# Revit family: Rohrschelle Trabant Inox, M 8-M10, Gummi, V4A
name_source: partatom
category: HLS-Bauteile
revit_build: Autodesk Revit 2017 (Build: 20190507_1515(x64)
units: mm (PartAtom-declared; Revit-internal decimal feet)

## family parameters
Arbeitsebenenbasiert = Ja
Beim Laden mit Abzugskörper schneiden = Nein
Bemaßung runder Anschluss = Durchmesser verwenden
Gemeinsam genutzt = Ja
Immer vertikal = Nein
Raumberechnungspunkt = Nein
Teiletyp = Normal

## types (11) — shared parameters
Anschluss = M8/M10
Bauart = zweiteilig
Baustoffklasse = B2
DS = 5 mm  [stored 0.0164042 ft]
DVS = 5 mm  [stored 0.0164042 ft]
Dämmstärke = 5 mm  [stored 0.0164042 ft]
Fabrikat = MEFA
Farbe Schalldämmeinlage = schwarz
Firma = MEFA Befestigungs- und Montagesysteme GmbH
H1 = 2 mm  [stored 0.00656168 ft]
HGA = 17 mm
Material = Edelstahl
Material Schalldämmeinlage = TPE
Mengeneinheit = St
Schalldämmeinlage = Gummi
Verschluss = Rastverschluss
Verschluss-Schraube = M6
Vorgabe-Ansicht = 1219 mm
max. Temperaturbeständigkeit = 100 °C
max. zul. Last horizontal = 0.00 kN
max. zul. Last vertikal = 0.00 kN
zero-valued in all types: Nennweite DN Rohr, Rohraußendurchmesser

## per-type parameters (varying)
- Trabant Inox, M8/M10, Ø 12- 15, Gummi, V4A: A=23 mm  [stored 0.0754593 ft]; AB=3 mm  [stored 0.00984252 ft]; Achsabstand=42 mm; Anschlußhöhe=22 mm; Artikelnummer=051003015; B=59 mm; Breite Material=20 mm; D=15 mm  [stored 0.0492126 ft]; D0=24 mm  [stored 0.0787402 ft]; DF1=17 mm; DF2=16 mm  [stored 0.0524934 ft]; Dmax=15 mm  [stored 0.0492126 ft]; Dmin=12 mm  [stored 0.0393701 ft]; EAN=4250928453839; Gewicht=0.05 kg; Gewicht pro Bauteil=0.05 kg; H=43 mm  [stored 0.141076 ft]; H2=4 mm  [stored 0.0131234 ft]; Kurztext1=Rohrschelle Trabant Inox 20x1,0; Kurztext2=12 - 15 mm M8/M10 TPE; MB=20 mm  [stored 0.0656168 ft]; MD=1 mm  [stored 0.00328084 ft]; Materialmaße=20x1,0 mm; R=12 mm  [stored 0.0393701 ft]; RM=15 mm  [stored 0.0492126 ft]; S=42 mm  [stored 0.137795 ft]; Stärke Material=1 mm  [stored 0.00328084 ft]; max. Rohraußendurchmesser=15 mm  [stored 0.0492126 ft]; min. Rohraußendurchmesser=12 mm  [stored 0.0393701 ft]; vpe=100 St
- Trabant Inox, M8/M10, Ø 16- 20, Gummi, V4A: A=23 mm  [stored 0.0754593 ft]; AB=4 mm  [stored 0.0131234 ft]; Achsabstand=46,5 mm; Anschlußhöhe=22 mm; Artikelnummer=051003020; B=64 mm; Breite Material=20 mm; D=20 mm  [stored 0.0656168 ft]; D0=29 mm  [stored 0.0951444 ft]; DF1=17 mm; DF2=16 mm  [stored 0.0524934 ft]; Dmax=20 mm  [stored 0.0656168 ft]; Dmin=16 mm  [stored 0.0524934 ft]; EAN=4250928453846; Gewicht=0.05 kg; Gewicht pro Bauteil=0.05 kg; H=48 mm  [stored 0.15748 ft]; H2=5 mm  [stored 0.0164042 ft]; Kurztext1=Rohrschelle Trabant Inox 20x1,0; Kurztext2=16 - 20 mm M8/M10 TPE; MB=20 mm  [stored 0.0656168 ft]; MD=1 mm  [stored 0.00328084 ft]; Materialmaße=20x1,0 mm; R=15 mm  [stored 0.0492126 ft]; RM=18 mm  [stored 0.0590551 ft]; Rohraußendurchmesser Zoll=3/8 Zoll; S=47 mm  [stored 0.154199 ft]; Stärke Material=1 mm  [stored 0.00328084 ft]; max. Rohraußendurchmesser=20 mm  [stored 0.0656168 ft]; min. Rohraußendurchmesser=16 mm  [stored 0.0524934 ft]; vpe=100 St
- Trabant Inox, M8/M10, Ø 21- 25, Gummi, V4A: A=23 mm  [stored 0.0754593 ft]; AB=4 mm  [stored 0.0131234 ft]; Achsabstand=51,5 mm; Anschlußhöhe=22 mm; Artikelnummer=051003025; B=69 mm; Breite Material=20 mm; D=25 mm  [stored 0.082021 ft]; D0=34 mm; DF1=17 mm; DF2=16 mm  [stored 0.0524934 ft]; Dmax=25 mm  [stored 0.082021 ft]; Dmin=21 mm  [stored 0.0688976 ft]; EAN=4250928453853; Gewicht=0.06 kg; Gewicht pro Bauteil=0.06 kg; H=53 mm  [stored 0.173885 ft]; H2=5 mm  [stored 0.0164042 ft]; Kurztext1=Rohrschelle Trabant Inox 20x1,0; Kurztext2=21 - 25 mm M8/M10 TPE; MB=20 mm  [stored 0.0656168 ft]; MD=1 mm  [stored 0.00328084 ft]; Materialmaße=20x1,0 mm; R=17 mm; RM=20 mm  [stored 0.0656168 ft]; Rohraußendurchmesser Zoll=1/2 Zoll; S=52 mm; Stärke Material=1 mm  [stored 0.00328084 ft]; max. Rohraußendurchmesser=25 mm  [stored 0.082021 ft]; min. Rohraußendurchmesser=21 mm  [stored 0.0688976 ft]; vpe=100 St
- Trabant Inox, M8/M10, Ø 26- 30, Gummi, V4A: A=23 mm  [stored 0.0754593 ft]; AB=4 mm  [stored 0.0131234 ft]; Achsabstand=57,0 mm; Anschlußhöhe=22 mm; Artikelnummer=051003030; B=74 mm; Breite Material=20 mm; D=30 mm  [stored 0.0984252 ft]; D0=39 mm  [stored 0.127953 ft]; DF1=17 mm; DF2=16 mm  [stored 0.0524934 ft]; Dmax=30 mm  [stored 0.0984252 ft]; Dmin=26 mm; EAN=4250928453860; Gewicht=0.06 kg; Gewicht pro Bauteil=0.06 kg; H=58 mm; H2=5 mm  [stored 0.0164042 ft]; Kurztext1=Rohrschelle Trabant Inox 20x1,0; Kurztext2=26 - 30 mm M8/M10 TPE; MB=20 mm  [stored 0.0656168 ft]; MD=1 mm  [stored 0.00328084 ft]; Materialmaße=20x1,0 mm; R=20 mm  [stored 0.0656168 ft]; RM=23 mm  [stored 0.0754593 ft]; Rohraußendurchmesser Zoll=3/4 Zoll; S=57 mm  [stored 0.187008 ft]; Stärke Material=1 mm  [stored 0.00328084 ft]; max. Rohraußendurchmesser=30 mm  [stored 0.0984252 ft]; min. Rohraußendurchmesser=26 mm; vpe=100 St
- Trabant Inox, M8/M10, Ø 32- 37, Gummi, V4A: A=23 mm  [stored 0.0754593 ft]; AB=5 mm  [stored 0.0164042 ft]; Achsabstand=64,0 mm; Anschlußhöhe=22 mm; Artikelnummer=051003037; B=81 mm; Breite Material=20 mm; D=37 mm  [stored 0.121391 ft]; D0=46 mm  [stored 0.150919 ft]; DF1=17 mm; DF2=16 mm  [stored 0.0524934 ft]; Dmax=37 mm  [stored 0.121391 ft]; Dmin=32 mm  [stored 0.104987 ft]; EAN=4250928453877; Gewicht=0.07 kg; Gewicht pro Bauteil=0.07 kg; H=65 mm; H2=5 mm  [stored 0.0164042 ft]; Kurztext1=Rohrschelle Trabant Inox 20x1,0; Kurztext2=32 - 37 mm M8/M10 TPE; MB=20 mm  [stored 0.0656168 ft]; MD=1 mm  [stored 0.00328084 ft]; Materialmaße=20x1,0 mm; R=23 mm  [stored 0.0754593 ft]; RM=27 mm; Rohraußendurchmesser Zoll=1 Zoll; S=64 mm; Stärke Material=1 mm  [stored 0.00328084 ft]; max. Rohraußendurchmesser=37 mm  [stored 0.121391 ft]; min. Rohraußendurchmesser=32 mm  [stored 0.104987 ft]; vpe=100 St
- Trabant Inox, M8/M10, Ø 42- 46, Gummi, V4A: A=23 mm  [stored 0.0754593 ft]; AB=4 mm  [stored 0.0131234 ft]; Achsabstand=74,0 mm; Anschlußhöhe=22,5 mm; Artikelnummer=051003046; B=92 mm; Breite Material=20 mm; D=46 mm  [stored 0.150919 ft]; D0=55 mm  [stored 0.180446 ft]; DF1=18 mm  [stored 0.0590551 ft]; DF2=17 mm; Dmax=46 mm  [stored 0.150919 ft]; Dmin=42 mm  [stored 0.137795 ft]; EAN=4250928453884; Gewicht=0.10 kg; Gewicht pro Bauteil=0.10 kg; H=75 mm; H2=5 mm  [stored 0.0164042 ft]; Kurztext1=Rohrschelle Trabant Inox 20x1,5; Kurztext2=42 - 46 mm M8/M10 TPE; MB=20 mm  [stored 0.0656168 ft]; MD=2 mm  [stored 0.00656168 ft]; Materialmaße=20x1,5 mm; R=28 mm; RM=31 mm  [stored 0.101706 ft]; Rohraußendurchmesser Zoll=1 1/4 Zoll; S=75 mm; Stärke Material=2 mm  [stored 0.00656168 ft]; max. Rohraußendurchmesser=46 mm  [stored 0.150919 ft]; min. Rohraußendurchmesser=42 mm  [stored 0.137795 ft]; vpe=50 St
- Trabant Inox, M8/M10, Ø 48- 52, Gummi, V4A: A=23 mm  [stored 0.0754593 ft]; AB=4 mm  [stored 0.0131234 ft]; Achsabstand=80,5 mm; Anschlußhöhe=22,5 mm; Artikelnummer=051003052; B=98 mm; Breite Material=20 mm; D=52 mm; D0=61 mm; DF1=18 mm  [stored 0.0590551 ft]; DF2=17 mm; Dmax=52 mm; Dmin=48 mm  [stored 0.15748 ft]; EAN=4250928453891; Gewicht=0.10 kg; Gewicht pro Bauteil=0.10 kg; H=81 mm; H2=5 mm  [stored 0.0164042 ft]; Kurztext1=Rohrschelle Trabant Inox 20x1,5; Kurztext2=48 - 52 mm M8/M10 TPE; MB=20 mm  [stored 0.0656168 ft]; MD=2 mm  [stored 0.00656168 ft]; Materialmaße=20x1,5 mm; R=31 mm  [stored 0.101706 ft]; RM=34 mm; Rohraußendurchmesser Zoll=1 1/2 Zoll; S=81 mm; Stärke Material=2 mm  [stored 0.00656168 ft]; max. Rohraußendurchmesser=52 mm; min. Rohraußendurchmesser=48 mm  [stored 0.15748 ft]; vpe=50 St
- Trabant Inox, M8/M10, Ø 54- 58, Gummi, V4A: A=23 mm  [stored 0.0754593 ft]; AB=4 mm  [stored 0.0131234 ft]; Achsabstand=86,5 mm; Anschlußhöhe=22,5 mm; Artikelnummer=051003058; B=104 mm; Breite Material=20 mm; D=58 mm; D0=67 mm; DF1=18 mm  [stored 0.0590551 ft]; DF2=17 mm; Dmax=58 mm; Dmin=54 mm  [stored 0.177165 ft]; EAN=4250928453907; Gewicht=0.11 kg; Gewicht pro Bauteil=0.11 kg; H=87 mm; H2=5 mm  [stored 0.0164042 ft]; Kurztext1=Rohrschelle Trabant Inox 20x1,5; Kurztext2=54 - 58 mm M8/M10 TPE; MB=20 mm  [stored 0.0656168 ft]; MD=2 mm  [stored 0.00656168 ft]; Materialmaße=20x1,5 mm; R=34 mm; RM=37 mm  [stored 0.121391 ft]; S=87 mm; Stärke Material=2 mm  [stored 0.00656168 ft]; max. Rohraußendurchmesser=58 mm; min. Rohraußendurchmesser=54 mm  [stored 0.177165 ft]; vpe=50 St
- Trabant Inox, M8/M10, Ø 60- 65, Gummi, V4A: A=23 mm  [stored 0.0754593 ft]; AB=5 mm  [stored 0.0164042 ft]; Achsabstand=93,5 mm; Anschlußhöhe=22,5 mm; Artikelnummer=051003065; B=111 mm; Breite Material=20 mm; D=65 mm; D0=74 mm; DF1=18 mm  [stored 0.0590551 ft]; DF2=17 mm; Dmax=65 mm; Dmin=60 mm; EAN=4250928453914; Gewicht=0.12 kg; Gewicht pro Bauteil=0.12 kg; H=94 mm; H2=6 mm  [stored 0.019685 ft]; Kurztext1=Rohrschelle Trabant Inox 20x1,5; Kurztext2=60 - 65 mm M8/M10 TPE; MB=20 mm  [stored 0.0656168 ft]; MD=2 mm  [stored 0.00656168 ft]; Materialmaße=20x1,5 mm; R=37 mm  [stored 0.121391 ft]; RM=41 mm  [stored 0.134514 ft]; Rohraußendurchmesser Zoll=2 Zoll; S=94 mm; Stärke Material=2 mm  [stored 0.00656168 ft]; max. Rohraußendurchmesser=65 mm; min. Rohraußendurchmesser=60 mm; vpe=50 St
- Trabant Inox, M8/M10, Ø 70- 76, Gummi, V4A: A=23 mm  [stored 0.0754593 ft]; AB=6 mm  [stored 0.019685 ft]; Achsabstand=104,0 mm; Anschlußhöhe=22,5 mm; Artikelnummer=051003076; B=122 mm; Breite Material=25 mm; D=76 mm; D0=85 mm; DF1=18 mm  [stored 0.0590551 ft]; DF2=17 mm; Dmax=76 mm; Dmin=70 mm; EAN=4250928453921; Gewicht=0.15 kg; Gewicht pro Bauteil=0.15 kg; H=105 mm; H2=6 mm  [stored 0.019685 ft]; Kurztext1=Rohrschelle Trabant Inox 25x1,5; Kurztext2=70 - 76 mm M8/M10 TPE; MB=25 mm  [stored 0.082021 ft]; MD=2 mm  [stored 0.00656168 ft]; Materialmaße=25x1,5 mm; R=43 mm  [stored 0.141076 ft]; RM=47 mm  [stored 0.154199 ft]; S=105 mm; Stärke Material=2 mm  [stored 0.00656168 ft]; max. Rohraußendurchmesser=76 mm; min. Rohraußendurchmesser=70 mm; vpe=50 St
- Trabant Inox, M8/M10, Ø 85- 90, Gummi, V4A: A=24 mm  [stored 0.0787402 ft]; AB=5 mm  [stored 0.0164042 ft]; Achsabstand=119,9 mm; Anschlußhöhe=235 mm; Artikelnummer=051003090; B=134 mm; Breite Material=25 mm; D=90 mm; D0=99 mm; DF1=14 mm  [stored 0.0459318 ft]; DF2=17 mm; Dmax=90 mm; Dmin=85 mm; EAN=4250928453938; Gewicht=0.21 kg; Gewicht pro Bauteil=0.21 kg; H=120 mm; H2=6 mm  [stored 0.019685 ft]; Kurztext1=Rohrschelle Trabant Inox 25x2,0; Kurztext2=85 - 90 mm M8/M10 TPE; MB=25 mm  [stored 0.082021 ft]; MD=2 mm  [stored 0.00656168 ft]; Materialmaße=25x2,0 mm; R=50 mm  [stored 0.164042 ft]; RM=54 mm  [stored 0.177165 ft]; Rohraußendurchmesser Zoll=3 Zoll; S=120 mm; Stärke Material=2 mm  [stored 0.00656168 ft]; max. Rohraußendurchmesser=90 mm; min. Rohraußendurchmesser=85 mm; vpe=50 St

note: [stored X ft] marks values corroborated as IEEE doubles in the binary element streams (Revit-internal decimal feet)

## geometry (parser evidence)
native form markers: Sweep x3
no freeform markers — native parametric forms only
